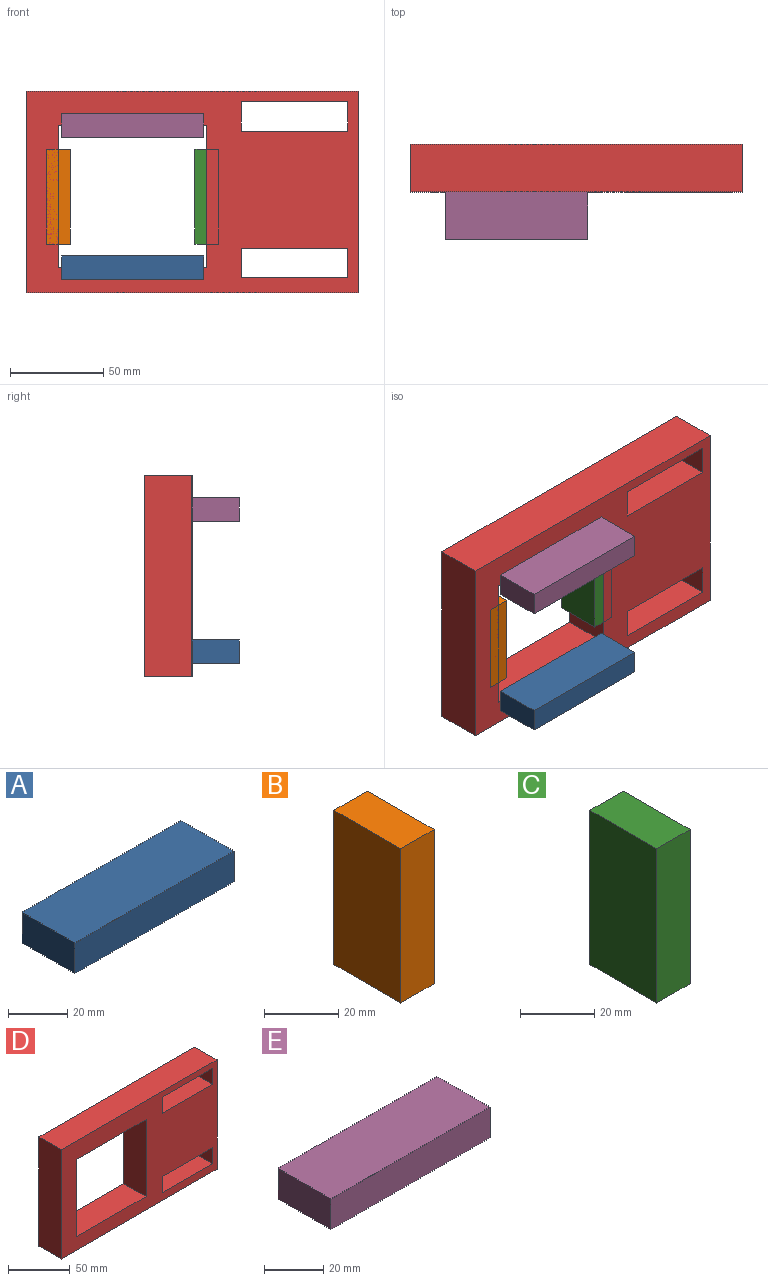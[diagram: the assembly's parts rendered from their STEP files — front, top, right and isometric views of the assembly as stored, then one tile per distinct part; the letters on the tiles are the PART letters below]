
ASSEMBLY  parts=5 mates=4
PART A: 6 faces, bbox 76.2x25.4x12.7 mm
  f0: plane 25.4x12.7mm, normal (-1,0,0), area 322.6mm2, adj f1,f3,f4,f5
  f1: plane 76.2x25.4mm, normal (0,0,-1), area 1935.5mm2, adj f0,f2,f4,f5
  f2: plane 25.4x12.7mm, normal (1,0,0), area 322.6mm2, adj f1,f3,f4,f5
  f3: plane 76.2x25.4mm, normal (0,0,1), area 1935.5mm2, adj f0,f2,f4,f5
  f4: plane 76.2x12.7mm, normal (0,-1,0), area 967.7mm2, adj f0,f1,f2,f3
  f5: plane 76.2x12.7mm, normal (0,1,0), area 967.7mm2, adj f0,f1,f2,f3
PART B: 6 faces, bbox 12.7x25.4x50.8 mm
  f0: plane 50.8x25.4mm, normal (-1,0,0), area 1290.3mm2, adj f1,f3,f4,f5
  f1: plane 25.4x12.7mm, normal (0,0,-1), area 322.6mm2, adj f0,f2,f4,f5
  f2: plane 50.8x25.4mm, normal (1,0,0), area 1290.3mm2, adj f1,f3,f4,f5
  f3: plane 25.4x12.7mm, normal (0,0,1), area 322.6mm2, adj f0,f2,f4,f5
  f4: plane 50.8x12.7mm, normal (0,-1,0), area 645.2mm2, adj f0,f1,f2,f3
  f5: plane 50.8x12.7mm, normal (0,1,0), area 645.2mm2, adj f0,f1,f2,f3
PART C: 6 faces, bbox 12.7x25.4x50.8 mm
  f0: plane 50.8x25.4mm, normal (-1,0,0), area 1290.3mm2, adj f1,f3,f4,f5
  f1: plane 25.4x12.7mm, normal (0,0,-1), area 322.6mm2, adj f0,f2,f4,f5
  f2: plane 50.8x25.4mm, normal (1,0,0), area 1290.3mm2, adj f1,f3,f4,f5
  f3: plane 25.4x12.7mm, normal (0,0,1), area 322.6mm2, adj f0,f2,f4,f5
  f4: plane 50.8x12.7mm, normal (0,-1,0), area 645.2mm2, adj f0,f1,f2,f3
  f5: plane 50.8x12.7mm, normal (0,1,0), area 645.2mm2, adj f0,f1,f2,f3
PART D: 18 faces, bbox 177.8x25.4x108 mm
  f0: plane 76.2x25.4mm, normal (1,0,0), area 1935.5mm2, adj f1,f15,f16,f17
  f1: plane 79.38x25.4mm, normal (0,0,-1), area 2016.1mm2, adj f0,f2,f16,f17
  f2: plane 76.2x25.4mm, normal (-1,0,0), area 1935.5mm2, adj f1,f15,f16,f17
  f3: plane 107.95x25.4mm, normal (-1,0,0), area 2741.9mm2, adj f4,f12,f16,f17
  f4: plane 177.8x25.4mm, normal (0,0,-1), area 4516.1mm2, adj f3,f5,f16,f17
  f5: plane 107.95x25.4mm, normal (1,0,0), area 2741.9mm2, adj f4,f12,f16,f17
  f6: plane 57.15x25.4mm, normal (0,0,1), area 1451.6mm2, adj f7,f13,f16,f17
  f7: plane 25.4x15.88mm, normal (1,0,0), area 403.2mm2, adj f6,f8,f16,f17
  f8: plane 57.15x25.4mm, normal (0,0,-1), area 1451.6mm2, adj f7,f13,f16,f17
  f9: plane 57.15x25.4mm, normal (0,0,1), area 1451.6mm2, adj f10,f14,f16,f17
  f10: plane 25.4x15.88mm, normal (1,0,0), area 403.2mm2, adj f9,f11,f16,f17
  f11: plane 57.15x25.4mm, normal (0,0,-1), area 1451.6mm2, adj f10,f14,f16,f17
  f12: plane 177.8x25.4mm, normal (0,0,1), area 4516.1mm2, adj f3,f5,f16,f17
  f13: plane 25.4x15.88mm, normal (-1,0,0), area 403.2mm2, adj f6,f8,f16,f17
  f14: plane 25.4x15.88mm, normal (-1,0,0), area 403.2mm2, adj f9,f11,f16,f17
  f15: plane 79.38x25.4mm, normal (0,0,1), area 2016.1mm2, adj f0,f2,f16,f17
  f16: plane 177.8x107.95mm, normal (0,-1,0), area 11330.6mm2, adj f0,f1,f2,f3,f4,f5,f6,f7
  f17: plane 177.8x107.95mm, normal (0,1,0), area 11330.6mm2, adj f0,f1,f2,f3,f4,f5,f6,f7
PART E: 6 faces, bbox 76.2x25.4x12.7 mm
  f0: plane 25.4x12.7mm, normal (-1,0,0), area 322.6mm2, adj f1,f3,f4,f5
  f1: plane 76.2x25.4mm, normal (0,0,-1), area 1935.5mm2, adj f0,f2,f4,f5
  f2: plane 25.4x12.7mm, normal (1,0,0), area 322.6mm2, adj f1,f3,f4,f5
  f3: plane 76.2x25.4mm, normal (0,0,1), area 1935.5mm2, adj f0,f2,f4,f5
  f4: plane 76.2x12.7mm, normal (0,-1,0), area 967.7mm2, adj f0,f1,f2,f3
  f5: plane 76.2x12.7mm, normal (0,1,0), area 967.7mm2, adj f0,f1,f2,f3
PLACE A t=(-37.99,-22.65,-157.28)mm
PLACE B t=(35.3,2.75,68.6)mm
PLACE C t=(25.07,2.75,69.01)mm
PLACE D t=(28.83,2.75,-41.37)mm
PLACE E t=(65.42,-22.65,-81.5)mm
MATE fastened E.f5 <-> D.f16  axis (0,1,0) through (24.29,-22.65,19.49)mm
MATE fastened B.f4 <-> D.f16  axis (0,-1,0) through (-15.4,-22.65,-18.61)mm
MATE fastened C.f4 <-> D.f16  axis (0,-1,0) through (63.98,-22.65,-18.61)mm
MATE fastened A.f5 <-> D.f16  axis (0,1,0) through (24.29,-22.65,-56.71)mm
